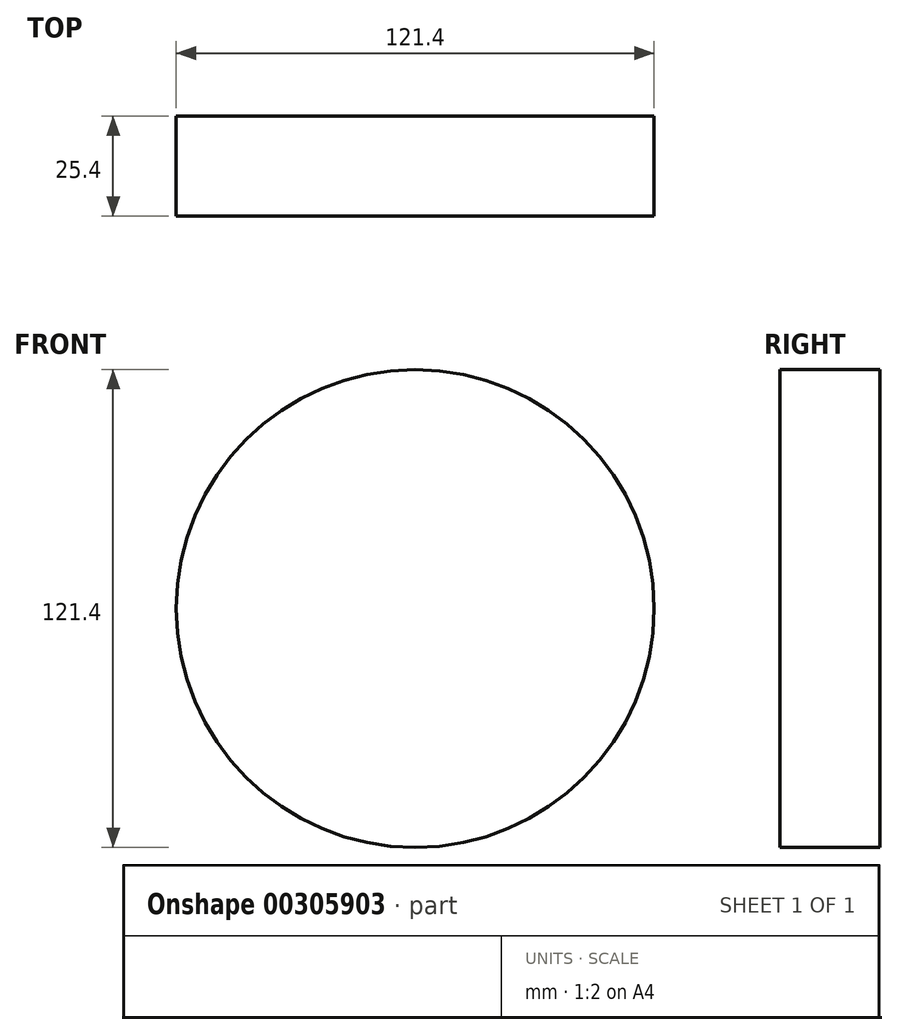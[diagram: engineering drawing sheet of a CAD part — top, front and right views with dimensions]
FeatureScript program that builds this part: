
annotation { "Feature Type Name" : "Feature", "Feature Type Description" : "" }
export const myFeature = defineFeature(function(context is Context, id is Id, definition is map)
    precondition{}
    {
        {
            var Q0;
            Q0=qCreatedBy(makeId("Front.planeOp"),FACE);
            var sketch = newSketch(context, id + "F0", { "sketchPlane" : qUnion([Q0])});
            skCircle(sketch, "E0", {"center": v(0, 0) * mm, "radius": 60.7 * mm});
            skCircle(sketch, "E1", {"center": v(0, 0) * mm, "radius": 50.5 * mm});
            skCircle(sketch, "E2", {"center": v(0, 0) * mm, "radius": 39.68 * mm});
            skCircle(sketch, "E3", {"center": v(0, 0) * mm, "radius": 30.19 * mm});
            skCircle(sketch, "E4", {"center": v(0, 0) * mm, "radius": 20.23 * mm});
            skCircle(sketch, "E5", {"center": v(0, 0) * mm, "radius": 9.01 * mm});
            skPoint(sketch, "E6", {"position": v(-11.95, 42.7) * mm});
            skPoint(sketch, "E7", {"position": v(23.83, 18.53) * mm});
            skPoint(sketch, "E8", {"position": v(26.82, -4.52) * mm});
            skPoint(sketch, "E9", {"position": v(-2.91, -27.25) * mm});
            skPoint(sketch, "E10", {"position": v(-10.2, -33.37) * mm});
            skPoint(sketch, "E11", {"position": v(0, -4.8) * mm});
            skPoint(sketch, "E12", {"position": v(4.08, 2.77) * mm});
            skPoint(sketch, "E13", {"position": v(-2.62, 3.35) * mm});
            skPoint(sketch, "E14", {"position": v(-30.08, 25.88) * mm});
            skPoint(sketch, "E15", {"position": v(-39.21, 6.07) * mm});
            skPoint(sketch, "E16", {"position": v(-44.3, 9.47) * mm});
            skPoint(sketch, "E17", {"position": v(-39.35, -21.13) * mm});
            skPoint(sketch, "E18", {"position": v(46.34, -4.8) * mm});
            skPoint(sketch, "E19", {"position": v(0, -36) * mm});
            skPoint(sketch, "E20", {"position": v(0, 55.53) * mm});
            skPoint(sketch, "E21", {"position": v(11.08, 70.1) * mm});
            skPoint(sketch, "E22", {"position": v(0, -50.5) * mm});
            skPoint(sketch, "E23", {"position": v(23.83, -36) * mm});
            skPoint(sketch, "E24", {"position": v(-10.25, 28.4) * mm});
            skPoint(sketch, "E25", {"position": v(-10.25, 33.89) * mm});
            skPoint(sketch, "E26", {"position": v(8.14, 18.53) * mm});
            skPoint(sketch, "E27", {"position": v(13.48, 32.93) * mm});
            skSolve(sketch);
        }
        {
            var Q0;
            Q0=makeQuery(id+"F0.imprint","IMPRINT",FACE,{"disambiguationData":[TD([[makeQuery(id+"F0.imprint","IMPRINT",EDGE,{"derivedFrom":sQuery(id+"F0.wireOp",EDGE,"E0")}),1.0]])]});
            var Q1;
            Q1=makeQuery(id+"F0.imprint","IMPRINT",FACE,{"disambiguationData":[TD([[makeQuery(id+"F0.imprint","IMPRINT",EDGE,{"derivedFrom":sQuery(id+"F0.wireOp",EDGE,"E1")}),1.0]])]});
            var Q2;
            Q2=makeQuery(id+"F0.imprint","IMPRINT",FACE,{"disambiguationData":[TD([[makeQuery(id+"F0.imprint","IMPRINT",EDGE,{"derivedFrom":sQuery(id+"F0.wireOp",EDGE,"E2")}),1.0]])]});
            var Q3;
            Q3=makeQuery(id+"F0.imprint","IMPRINT",FACE,{"disambiguationData":[TD([[makeQuery(id+"F0.imprint","IMPRINT",EDGE,{"derivedFrom":sQuery(id+"F0.wireOp",EDGE,"E3")}),1.0]])]});
            var Q4;
            Q4=makeQuery(id+"F0.imprint","IMPRINT",FACE,{"disambiguationData":[TD([[makeQuery(id+"F0.imprint","IMPRINT",EDGE,{"derivedFrom":sQuery(id+"F0.wireOp",EDGE,"E4")}),1.0]])]});
            var Q5;
            Q5=makeQuery(id+"F0.imprint","IMPRINT",FACE,{"disambiguationData":[TD([[makeQuery(id+"F0.imprint","IMPRINT",EDGE,{"derivedFrom":sQuery(id+"F0.wireOp",EDGE,"E5")}),1.0]])]});
            extrude(context, id + "F1", {"entities" : qUnion([Q0, Q1, Q2, Q3, Q4, Q5]), "depth" : 25.4 * mm});
        }
    });
